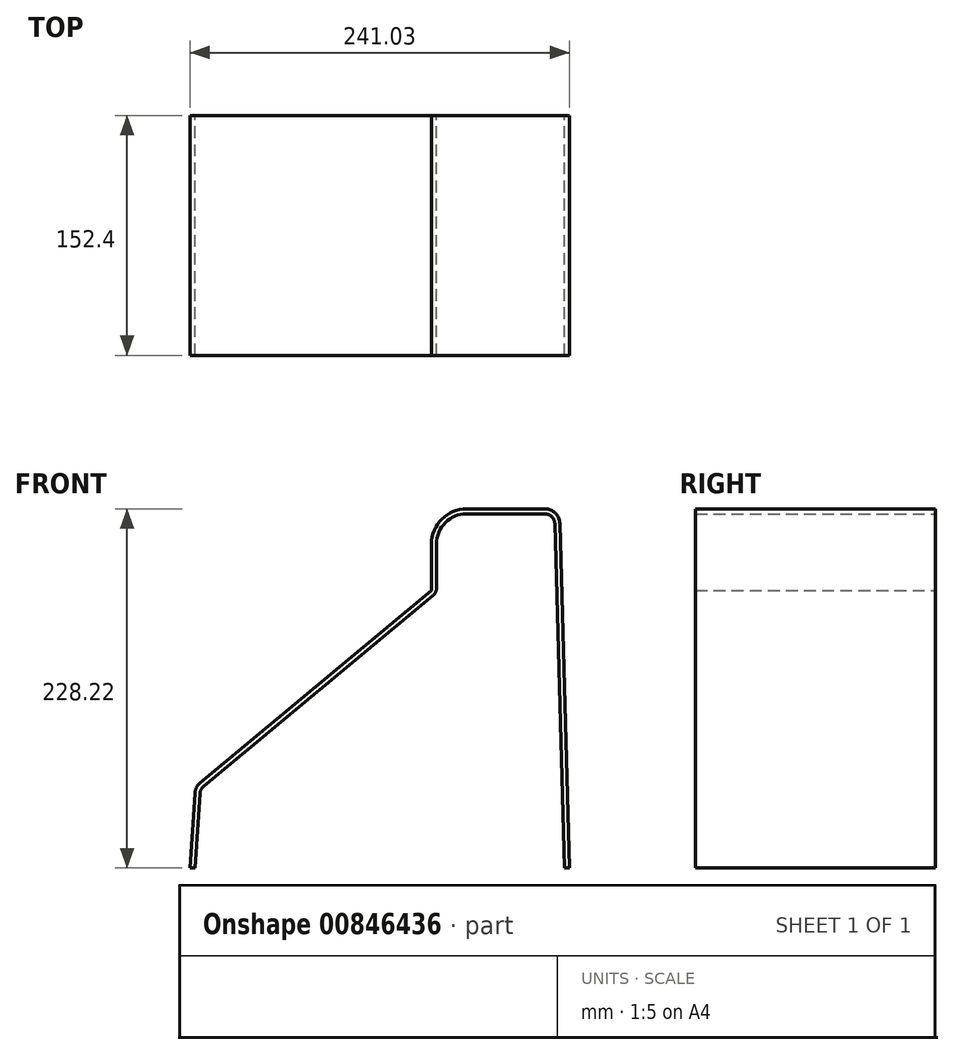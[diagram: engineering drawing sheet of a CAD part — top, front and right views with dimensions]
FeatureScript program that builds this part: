
annotation { "Feature Type Name" : "Feature", "Feature Type Description" : "" }
export const myFeature = defineFeature(function(context is Context, id is Id, definition is map)
    precondition{}
    {
        {
            var Q0;
            Q0=qCreatedBy(makeId("Front.planeOp"),FACE);
            var sketch = newSketch(context, id + "F0", { "sketchPlane" : qUnion([Q0])});
            skLineSegment(sketch, "E0", {"start": v(19.05, 0) * mm, "end": v(68.76, 0) * mm});
            skLineSegment(sketch, "E1", {"start": v(75.1, -6.17) * mm, "end": v(81.28, -225.04) * mm});
            skLineSegment(sketch, "E2", {"start": v(0, -19.05) * mm, "end": v(0, -47.06) * mm});
            skLineSegment(sketch, "E3", {"start": v(-2.29, -51.94) * mm, "end": v(-148.02, -173.26) * mm});
            skLineSegment(sketch, "E4", {"start": v(-150.3, -177.72) * mm, "end": v(-153.42, -225.04) * mm});
            skLineSegment(sketch, "E5", {"start": v(-150.11, -39.71) * mm, "end": v(-150.11, -590.32) * mm, "construction": true});
            skLineSegment(sketch, "E6", {"start": v(74.93, 140.82) * mm, "end": v(74.93, -443.69) * mm, "construction": true});
            skPoint(sketch, "E7.visualSharp", {"position": v(74.93, 0) * mm});
            skArc(sketch, "E7.filletArc", {"start": v(75.1, -6.17) * mm, "mid": v(73.18, -1.8) * mm, "end": v(68.76, 0) * mm});
            skPoint(sketch, "E8.visualSharp", {"position": v(0, -50.04) * mm});
            skArc(sketch, "E8.filletArc", {"start": v(-2.29, -51.94) * mm, "mid": v(-0.6, -49.76) * mm, "end": v(0, -47.06) * mm});
            skPoint(sketch, "E9.visualSharp", {"position": v(-150.11, -175) * mm});
            skArc(sketch, "E9.filletArc", {"start": v(-148.02, -173.26) * mm, "mid": v(-149.62, -175.26) * mm, "end": v(-150.3, -177.72) * mm});
            skPoint(sketch, "E10.visualSharp", {"position": v(0, 0) * mm});
            skArc(sketch, "E10.filletArc", {"start": v(19.05, 0) * mm, "mid": v(5.58, -5.58) * mm, "end": v(0, -19.05) * mm});
            skLineSegment(sketch, "E11.0", {"start": v(-153.46, -177.52) * mm, "end": v(-156.58, -224.83) * mm});
            skArc(sketch, "E11.1", {"start": v(-150.05, -170.82) * mm, "mid": v(-152.44, -173.82) * mm, "end": v(-153.46, -177.52) * mm});
            skLineSegment(sketch, "E11.2", {"start": v(-3.18, -48.55) * mm, "end": v(-150.05, -170.82) * mm});
            skLineSegment(sketch, "E11.3", {"start": v(-3.18, -19.05) * mm, "end": v(-3.18, -48.55) * mm});
            skLineSegment(sketch, "E11.4", {"start": v(78.28, -6.08) * mm, "end": v(84.45, -224.95) * mm});
            skArc(sketch, "E11.5", {"start": v(78.28, -6.08) * mm, "mid": v(75.4, 0.48) * mm, "end": v(68.76, 3.18) * mm});
            skLineSegment(sketch, "E11.6", {"start": v(19.05, 3.18) * mm, "end": v(68.76, 3.18) * mm});
            skArc(sketch, "E11.7", {"start": v(19.05, 3.18) * mm, "mid": v(3.33, -3.33) * mm, "end": v(-3.18, -19.05) * mm});
            skLineSegment(sketch, "E12", {"start": v(-153.42, -225.04) * mm, "end": v(-156.58, -224.83) * mm});
            skLineSegment(sketch, "E13", {"start": v(84.45, -224.95) * mm, "end": v(81.28, -225.04) * mm});
            skSolve(sketch);
        }
        {
            var Q0;
            Q0 = qSketchRegion(id + "F0", true);
            extrude(context, id + "F1", {"entities" : qUnion([Q0]), "depth" : 152.4 * mm, "offsetDistance" : 25.4 * mm});
        }
    });
